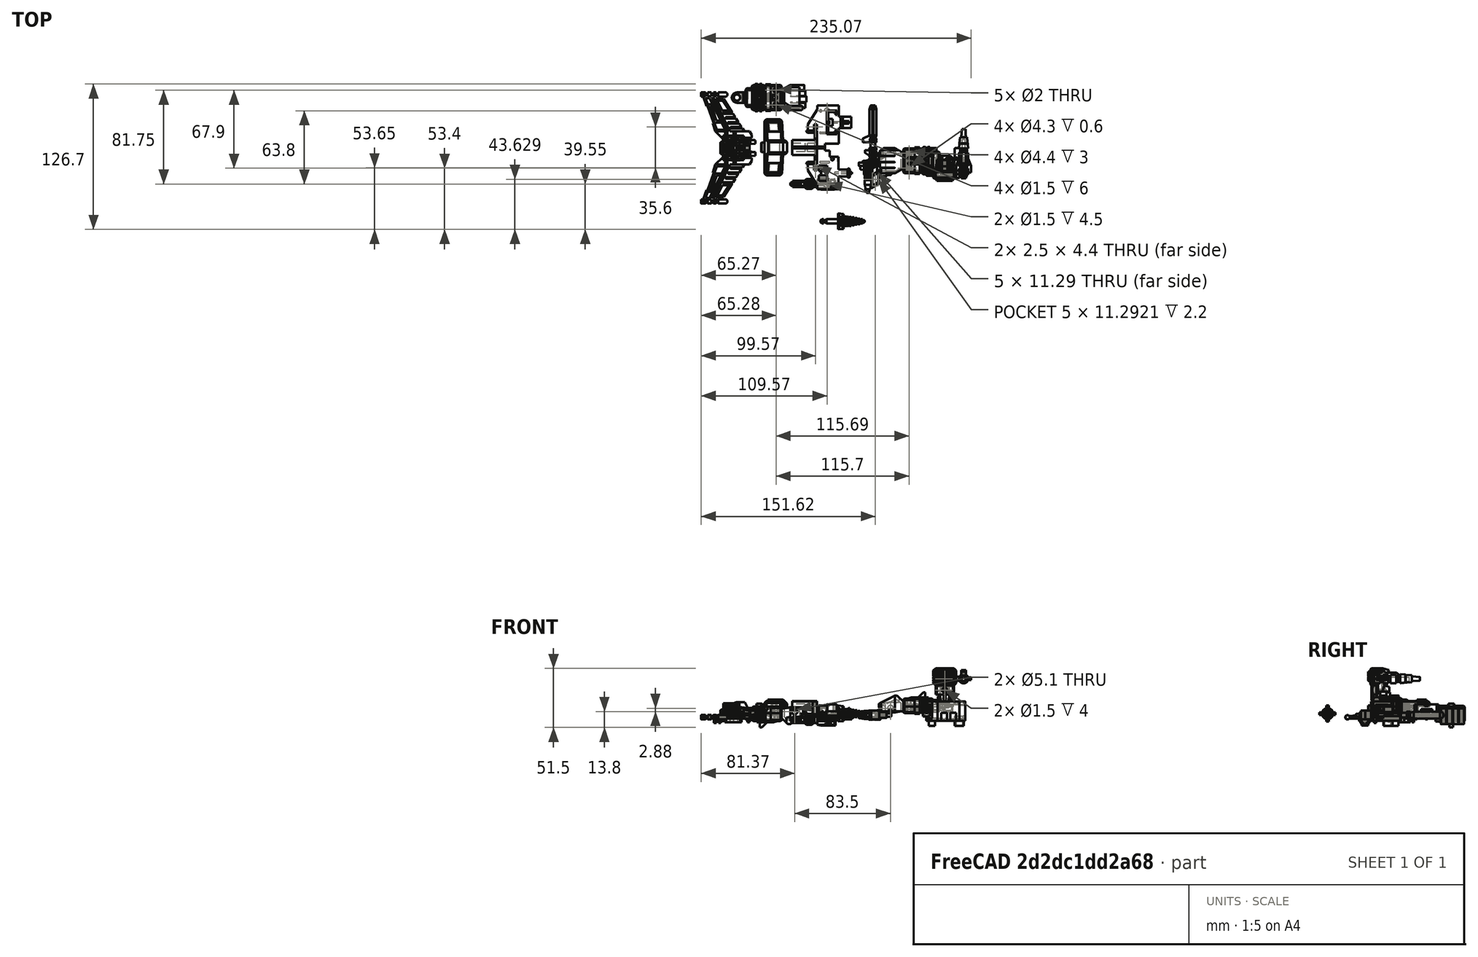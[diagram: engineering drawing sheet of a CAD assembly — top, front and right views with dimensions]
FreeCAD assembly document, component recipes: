
FREECAD ASSEMBLY — COMPONENT RECIPES ("Accesories2")

This assembly document has 7 components, labeled P0..P6 below (a component is one placed body or linked part). 2 of them carry a construction recipe — the FreeCAD feature program that regenerates the part from scratch, quoted from this document or its linked companion documents; the rest are supplied as boundary geometry only. No exploded tour is included for this assembly.
COMPONENT P0 — recipe-attached ("Waist", modeled in this document).
Construction recipe (the document's own serialized feature program — sketch geometry with constraints, then the solid features built on it; lengths are millimeters unless a unit is written):

FEATURE [Sketcher::SketchObject] Sketch571
  ArcFitTolerance = 1e-06
  AttachmentSupport = -> [XY_Plane035]
  FullyConstrained = true
  MakeInternals = false
  MapMode = 5
  sketch-geometry (4):
    g0: LineSegment StartX=0 StartY=0 StartZ=0 EndX=49 EndY=0 EndZ=0
    g1: LineSegment StartX=49 StartY=0 StartZ=0 EndX=49 EndY=15 EndZ=0
    g2: LineSegment StartX=49 StartY=15 StartZ=0 EndX=0 EndY=15 EndZ=0
    g3: LineSegment StartX=0 StartY=15 StartZ=0 EndX=0 EndY=0 EndZ=0
  constraints (11):
    c: Coincident(g0,g1)
    c: Coincident(g1,g2)
    c: Coincident(g2,g3)
    c: Coincident(g3,g0)
    c: Horizontal(g0)
    c: Horizontal(g2)
    c: Vertical(g1)
    c: Vertical(g3)
    c: Coincident(g0,g-1)
    c: DistanceY(g3,g3) = 15
    c: DistanceX(g2,g2) = 49
FEATURE [PartDesign::Pad] Pad410
  Direction = (0,0,1)
  Length = 4.75
  Length2 = 10
  Profile = -> Sketch571
  ReferenceAxis = -> Sketch571 [N_Axis]
  Refine = true
  Suppressed = false
  Type = 0
FEATURE [Sketcher::SketchObject] Sketch572
  ArcFitTolerance = 1e-06
  AttachmentSupport = -> [Pad410]
  ExternalGeometry = -> [Pad410]
  FullyConstrained = true
  MakeInternals = false
  MapMode = 5
  Placement = pos=(0,0,4.75) rot=(0,0,1;0rad)
  sketch-geometry (4):
    g0: LineSegment StartX=0 StartY=0 StartZ=0 EndX=18.55 EndY=-1.3 EndZ=0
    g1: LineSegment StartX=18.55 StartY=-1.3 StartZ=0 EndX=30.45 EndY=-1.3 EndZ=0
    g2: LineSegment StartX=30.45 StartY=-1.3 StartZ=0 EndX=49 EndY=0 EndZ=0
    g3: LineSegment StartX=0 StartY=0 StartZ=0 EndX=49 EndY=0 EndZ=0
  constraints (11):
    c: Coincident(g0,g-1)
    c: Coincident(g1,g0)
    c: Horizontal(g1)
    c: Coincident(g2,g1)
    c: Coincident(g2,g-3)
    c: DistanceY(g0,g0) = 1.3
    c: DistanceX(g1,g1) = 11.9
    c: DistanceX(g0,g2) = 49
    c: DistanceX(g0,g0) = 18.55
    c: Coincident(g3,g0)
    c: Coincident(g3,g2)
FEATURE [PartDesign::Pad] Pad411
  BaseFeature = -> Pad410
  Direction = (0,0,1)
  Length = 4.75
  Length2 = 10
  Profile = -> Sketch572
  ReferenceAxis = -> Sketch572 [N_Axis]
  Refine = true
  Reversed = true
  Suppressed = false
  Type = 0
FEATURE [Sketcher::SketchObject] Sketch573
  ArcFitTolerance = 1e-06
  AttachmentSupport = -> [Pad411]
  ExternalGeometry = -> [Pad411]
  FullyConstrained = true
  MakeInternals = false
  MapMode = 5
  Placement = pos=(0,0,4.75) rot=(0,0,1;0rad)
  sketch-geometry (4):
    g0: LineSegment StartX=18.55 StartY=-4.7 StartZ=0 EndX=30.45 EndY=-4.7 EndZ=0
    g1: LineSegment StartX=30.45 StartY=-4.7 StartZ=0 EndX=30.45 EndY=15 EndZ=0
    g2: LineSegment StartX=30.45 StartY=15 StartZ=0 EndX=18.55 EndY=15 EndZ=0
    g3: LineSegment StartX=18.55 StartY=15 StartZ=0 EndX=18.55 EndY=-4.7 EndZ=0
  constraints (12):
    c: Coincident(g0,g1)
    c: Coincident(g1,g2)
    c: Coincident(g2,g3)
    c: Coincident(g3,g0)
    c: Horizontal(g0)
    c: Horizontal(g2)
    c: Vertical(g1)
    c: Vertical(g3)
    c: PointOnObject(g1,g-4)
    c: PointOnObject(g-3,g3)
    c: PointOnObject(g-3,g1)
    c: DistanceY(g3,g3) = 19.7
FEATURE [PartDesign::Pad] Pad412
  BaseFeature = -> Pad411
  Direction = (0,0,1)
  Length = 4.75
  Length2 = 10
  Profile = -> Sketch573
  ReferenceAxis = -> Sketch573 [N_Axis]
  Refine = true
  Reversed = true
  Suppressed = false
  Type = 0
FEATURE [PartDesign::Pad] Pad413
  BaseFeature = -> Pad412
  Direction = (0,0,1)
  Length = 1.5
  Length2 = 10
  Profile = -> Sketch573
  ReferenceAxis = -> Sketch573 [N_Axis]
  Refine = true
  Suppressed = false
  Type = 0
FEATURE [Sketcher::SketchObject] Sketch574
  ArcFitTolerance = 1e-06
  AttachmentSupport = -> [Pad413]
  ExternalGeometry = -> [Pad413]
  FullyConstrained = true
  MakeInternals = false
  MapMode = 5
  Placement = pos=(0,0,4.75) rot=(0,0,1;0rad)
  sketch-geometry (6):
    g0: LineSegment StartX=0 StartY=15 StartZ=0 EndX=18.55 EndY=15 EndZ=0
    g1: LineSegment StartX=30.45 StartY=15 StartZ=0 EndX=49 EndY=15 EndZ=0
    g2: LineSegment StartX=49 StartY=15 StartZ=0 EndX=30.45 EndY=14 EndZ=0
    g3: LineSegment StartX=30.45 StartY=14 StartZ=0 EndX=30.45 EndY=15 EndZ=0
    g4: LineSegment StartX=0 StartY=15 StartZ=0 EndX=18.55 EndY=14 EndZ=0
    g5: LineSegment StartX=18.55 StartY=14 StartZ=0 EndX=18.55 EndY=15 EndZ=0
  constraints (14):
    c: Coincident(g0,g-3)
    c: Coincident(g0,g-5)
    c: Coincident(g1,g-6)
    c: Coincident(g1,g-4)
    c: Coincident(g2,g1)
    c: PointOnObject(g2,g-6)
    c: Coincident(g3,g2)
    c: Coincident(g3,g1)
    c: Coincident(g4,g0)
    c: PointOnObject(g4,g-5)
    c: Coincident(g5,g4)
    c: Coincident(g5,g0)
    c: DistanceY(g5,g5) = 1
    c: DistanceY(g3,g3) = 1
FEATURE [PartDesign::Pocket] Pocket255
  BaseFeature = -> Pad413
  Direction = (0,0,-1)
  Length = 3.25
  Length2 = 5
  Profile = -> Sketch574
  ReferenceAxis = -> Sketch574 [N_Axis]
  Refine = true
  Suppressed = false
  Type = 0
FEATURE [Sketcher::SketchObject] Sketch575
  ArcFitTolerance = 1e-06
  AttachmentSupport = -> [Pocket255]
  ExternalGeometry = -> [Pocket255]
  FullyConstrained = true
  MakeInternals = false
  MapMode = 5
  Placement = pos=(0,0,4.75) rot=(0,0,1;0rad)
  sketch-geometry (12):
    g0: LineSegment StartX=2.7 StartY=12.1505 StartZ=0 EndX=10.95 EndY=11.7058 EndZ=0
    g1: LineSegment StartX=10.95 StartY=11.7058 StartZ=0 EndX=10.95 EndY=1.93924 EndZ=0
    g2: LineSegment StartX=10.95 StartY=1.93924 StartZ=0 EndX=2.7 EndY=2.5174 EndZ=0
    g3: LineSegment StartX=2.7 StartY=2.5174 StartZ=0 EndX=2.7 EndY=12.1505 EndZ=0
    g4: LineSegment StartX=46.3 StartY=12.1505 StartZ=0 EndX=38.05 EndY=11.7058 EndZ=0
    g5: LineSegment StartX=38.05 StartY=11.7058 StartZ=0 EndX=38.05 EndY=1.93924 EndZ=0
    g6: LineSegment StartX=38.05 StartY=1.93924 StartZ=0 EndX=46.3 EndY=2.5174 EndZ=0
    g7: LineSegment StartX=46.3 StartY=2.5174 StartZ=0 EndX=46.3 EndY=12.1505 EndZ=0
    g8: LineSegment [constr] StartX=40.9003 StartY=14.5634 StartZ=0 EndX=41.0457 EndY=11.8673 EndZ=0
    g9: LineSegment [constr] StartX=8.09969 StartY=14.5634 StartZ=0 EndX=7.95435 EndY=11.8673 EndZ=0
    g10: LineSegment [constr] StartX=7.95734 StartY=2.14896 StartZ=0 EndX=7.76858 EndY=-0.544429 EndZ=0
    g11: LineSegment [constr] StartX=41.0427 StartY=2.14896 StartZ=0 EndX=41.2314 EndY=-0.544429 EndZ=0
  constraints (40):
    c: Coincident(g1,g0)
    c: Vertical(g1)
    c: Coincident(g2,g1)
    c: Coincident(g3,g2)
    c: Coincident(g3,g0)
    c: Coincident(g5,g4)
    c: Vertical(g5)
    c: Coincident(g6,g5)
    c: Coincident(g7,g6)
    c: Coincident(g7,g4)
    c: Vertical(g7)
    c: Vertical(g3)
    c: Parallel(g-3,g0)
    c: Parallel(g-6,g2)
    c: Parallel(g4,g-4)
    c: Parallel(g6,g-5)
    c: DistanceX(g0,g0) = 8.25
    c: DistanceX(g4,g4) = 8.25
    c: DistanceX(g-3,g0) = 2.7
    c: DistanceX(g4,g-4) = 2.7
    c: PointOnObject(g8,g-4)
    c: PointOnObject(g8,g4)
    c: PointOnObject(g9,g-3)
    c: PointOnObject(g9,g0)
    c: Perpendicular(g9,g-3)
    c: Perpendicular(g8,g-4)
    c: Distance(g4,g8) = 3
    c: Distance(g0,g9) = 3
    c: Distance(g9) = 2.7
    c: Distance(g8) = 2.7
    c: PointOnObject(g10,g2)
    c: PointOnObject(g10,g-6)
    c: Perpendicular(g-6,g10)
    c: Distance(g10) = 2.7
    c: PointOnObject(g11,g6)
    c: PointOnObject(g11,g-5)
    c: Perpendicular(g11,g6)
    c: Distance(g11) = 2.7
    c: Distance(g5,g11) = 3
    c: Distance(g10,g1) = 3
FEATURE [PartDesign::Pad] Pad414
  BaseFeature = -> Pocket255
  Direction = (0,0,1)
  Length = 1.5
  Length2 = 10
  Profile = -> Sketch575
  ReferenceAxis = -> Sketch575 [N_Axis]
  Refine = true
  Suppressed = false
  Type = 0
FEATURE [PartDesign::Chamfer] Chamfer010
  Angle = 45
  Base = -> Pad414 [Edge3,Edge2,Edge29,Edge30,Edge52,Edge31,Edge43,Edge17,Edge5,Edge14]
  BaseFeature = -> Pad414
  ChamferType = 0
  FlipDirection = false
  Refine = true
  Size = 1.5
  Size2 = 1
  SupportTransform = false
  Suppressed = false
  UseAllEdges = false
FEATURE [PartDesign::Chamfer] Chamfer011
  Angle = 45
  Base = -> Chamfer010 [Edge48,Edge21]
  BaseFeature = -> Chamfer010
  ChamferType = 0
  FlipDirection = false
  Refine = true
  Size = 3.5
  Size2 = 1
  SupportTransform = false
  Suppressed = false
  UseAllEdges = false
FEATURE [PartDesign::Chamfer] Chamfer012
  Angle = 45
  Base = -> Chamfer011 [Edge26,Edge28,Edge30,Edge15,Edge13,Edge11]
  BaseFeature = -> Chamfer011
  ChamferType = 0
  FlipDirection = false
  Refine = true
  Size = 1.49
  Size2 = 1
  SupportTransform = false
  Suppressed = false
  UseAllEdges = false
FEATURE [Sketcher::SketchObject] Sketch576
  ArcFitTolerance = 1e-06
  AttachmentSupport = -> [Chamfer012]
  ExternalGeometry = -> [Chamfer012]
  FullyConstrained = true
  MakeInternals = false
  MapMode = 5
  Placement = pos=(0,0,1.5) rot=(0,0,1;0rad)
  sketch-geometry (6):
    g0: LineSegment StartX=0 StartY=13.5 StartZ=0 EndX=1.58304 EndY=15 EndZ=0
    g1: LineSegment StartX=1.58304 StartY=15 StartZ=0 EndX=0 EndY=15 EndZ=0
    g2: LineSegment StartX=0 StartY=15 StartZ=0 EndX=0 EndY=13.5 EndZ=0
    g3: LineSegment StartX=49 StartY=13.5 StartZ=0 EndX=47.417 EndY=15 EndZ=0
    g4: LineSegment StartX=47.417 StartY=15 StartZ=0 EndX=49 EndY=15 EndZ=0
    g5: LineSegment StartX=49 StartY=15 StartZ=0 EndX=49 EndY=13.5 EndZ=0
  constraints (14):
    c: Coincident(g0,g-5)
    c: PointOnObject(g0,g-3)
    c: PointOnObject(g-4,g0)
    c: Coincident(g1,g0)
    c: Coincident(g1,g-5)
    c: Coincident(g2,g1)
    c: Coincident(g2,g0)
    c: Coincident(g3,g-9)
    c: PointOnObject(g3,g-7)
    c: Coincident(g4,g3)
    c: Coincident(g4,g-8)
    c: Coincident(g5,g4)
    c: Coincident(g5,g3)
    c: PointOnObject(g-6,g3)
FEATURE [PartDesign::Pocket] Pocket256
  BaseFeature = -> Chamfer012
  Direction = (0,0,-1)
  Length = 5
  Length2 = 5
  Profile = -> Sketch576
  ReferenceAxis = -> Sketch576 [N_Axis]
  Refine = true
  Suppressed = false
  Type = 0
FEATURE [Sketcher::SketchObject] Sketch577
  ArcFitTolerance = 1e-06
  AttachmentSupport = -> [Pocket256]
  ExternalGeometry = -> [Pocket256]
  FullyConstrained = true
  MakeInternals = false
  MapMode = 5
  Placement = pos=(0,0,0) rot=(1,0,0;3.14159rad)
  sketch-geometry (4):
    g0: LineSegment StartX=1.5 StartY=-1.39856 StartZ=0 EndX=1.5 EndY=-12.4978 EndZ=0
    g1: LineSegment StartX=1.5 StartY=-12.4978 StartZ=0 EndX=47.5 EndY=-12.4978 EndZ=0
    g2: LineSegment StartX=47.5 StartY=-12.4978 StartZ=0 EndX=47.5 EndY=-1.39856 EndZ=0
    g3: LineSegment StartX=47.5 StartY=-1.39856 StartZ=0 EndX=1.5 EndY=-1.39856 EndZ=0
  constraints (10):
    c: Coincident(g0,g1)
    c: Coincident(g1,g2)
    c: Coincident(g2,g3)
    c: Coincident(g3,g0)
    c: Vertical(g0)
    c: Vertical(g2)
    c: Horizontal(g1)
    c: Coincident(g0,g-8)
    c: PointOnObject(g-4,g1)
    c: Coincident(g2,g-7)
FEATURE [PartDesign::Pocket] Pocket257
  BaseFeature = -> Pocket256
  Direction = (0,0,1)
  Length = 3.25
  Length2 = 5
  Profile = -> Sketch577
  ReferenceAxis = -> Sketch577 [N_Axis]
  Refine = true
  Suppressed = false
  Type = 0
FEATURE [Sketcher::SketchObject] Sketch578
  ArcFitTolerance = 1e-06
  AttachmentSupport = -> [Pocket257]
  ExternalGeometry = -> [Pocket257]
  FullyConstrained = true
  MakeInternals = false
  MapMode = 5
  Placement = pos=(0,0,0) rot=(1,0,0;3.14159rad)
  sketch-geometry (4):
    g0: LineSegment StartX=20.04 StartY=1.2 StartZ=0 EndX=20.04 EndY=-1.39856 EndZ=0
    g1: LineSegment StartX=20.04 StartY=-1.39856 StartZ=0 EndX=28.96 EndY=-1.39856 EndZ=0
    g2: LineSegment StartX=28.96 StartY=-1.39856 StartZ=0 EndX=28.96 EndY=1.2 EndZ=0
    g3: LineSegment StartX=28.96 StartY=1.2 StartZ=0 EndX=20.04 EndY=1.2 EndZ=0
  constraints (10):
    c: Coincident(g0,g1)
    c: Coincident(g1,g2)
    c: Coincident(g2,g3)
    c: Coincident(g3,g0)
    c: Vertical(g0)
    c: Vertical(g2)
    c: Horizontal(g1)
    c: Coincident(g0,g-3)
    c: PointOnObject(g1,g-4)
    c: Coincident(g2,g-3)
FEATURE [PartDesign::Pocket] Pocket258
  BaseFeature = -> Pocket257
  Direction = (0,0,1)
  Length = 3.25
  Length2 = 5
  Profile = -> Sketch578
  ReferenceAxis = -> Sketch578 [N_Axis]
  Refine = true
  Suppressed = false
  Type = 0
FEATURE [Sketcher::SketchObject] Sketch579
  ArcFitTolerance = 1e-06
  AttachmentSupport = -> [Pocket258]
  ExternalGeometry = -> [Pocket258]
  FullyConstrained = true
  MakeInternals = false
  MapMode = 5
  Placement = pos=(0,0,3.25) rot=(1,0,0;3.14159rad)
  sketch-geometry (12):
    g0: LineSegment StartX=20.04 StartY=1.2 StartZ=0 EndX=20.04 EndY=-12.4978 EndZ=0
    g1: LineSegment StartX=20.04 StartY=-12.4978 StartZ=0 EndX=28.96 EndY=-12.4978 EndZ=0
    g2: LineSegment StartX=28.96 StartY=-12.4978 StartZ=0 EndX=28.96 EndY=1.2 EndZ=0
    g3: LineSegment StartX=28.96 StartY=1.2 StartZ=0 EndX=20.04 EndY=1.2 EndZ=0
    g4: LineSegment StartX=3.7 StartY=-3.27724 StartZ=0 EndX=9.95 EndY=-2.83924 EndZ=0
    g5: LineSegment StartX=9.95 StartY=-2.83924 StartZ=0 EndX=9.95 EndY=-10.8058 EndZ=0
    g6: LineSegment StartX=9.95 StartY=-10.8058 StartZ=0 EndX=3.7 EndY=-11.1427 EndZ=0
    g7: LineSegment StartX=3.7 StartY=-11.1427 StartZ=0 EndX=3.7 EndY=-3.27724 EndZ=0
    g8: LineSegment StartX=39.05 StartY=-2.83924 StartZ=0 EndX=45.3 EndY=-3.27724 EndZ=0
    g9: LineSegment StartX=45.3 StartY=-3.27724 StartZ=0 EndX=45.3 EndY=-11.1427 EndZ=0
    g10: LineSegment StartX=45.3 StartY=-11.1427 StartZ=0 EndX=39.05 EndY=-10.8058 EndZ=0
    g11: LineSegment StartX=39.05 StartY=-10.8058 StartZ=0 EndX=39.05 EndY=-2.83924 EndZ=0
  constraints (34):
    c: Coincident(g0,g1)
    c: Coincident(g1,g2)
    c: Coincident(g2,g3)
    c: Coincident(g3,g0)
    c: Vertical(g0)
    c: Vertical(g2)
    c: Horizontal(g1)
    c: Coincident(g0,g-7)
    c: PointOnObject(g1,g-6)
    c: Coincident(g2,g-7)
    c: Coincident(g5,g4)
    c: Vertical(g5)
    c: Coincident(g6,g5)
    c: Coincident(g7,g6)
    c: Coincident(g7,g4)
    c: Vertical(g7)
    c: Coincident(g9,g8)
    c: Vertical(g9)
    c: Coincident(g10,g9)
    c: Coincident(g11,g10)
    c: Coincident(g11,g8)
    c: Vertical(g11)
    c: DistanceX(g-15,g8) = 1
    c: DistanceX(g8,g-15) = 1
    c: DistanceX(g4,g-9) = 1
    c: DistanceX(g-10,g4) = 1
    c: Parallel(g-8,g4)
    c: Parallel(g6,g-11)
    c: Parallel(g8,g-15)
    c: Parallel(g10,g-14)
    c: DistanceY(g-14,g10) = 0.9
    c: DistanceY(g8,g-15) = 0.9
    c: DistanceY(g4,g-9) = 0.9
    c: DistanceY(g-11,g5) = 0.9
FEATURE [PartDesign::Pocket] Pocket259
  BaseFeature = -> Pocket258
  Direction = (0,0,1)
  Length = 1.5
  Length2 = 5
  Profile = -> Sketch579
  ReferenceAxis = -> Sketch579 [N_Axis]
  Refine = true
  Suppressed = false
  Type = 0
FEATURE [Sketcher::SketchObject] Sketch580
  ArcFitTolerance = 1e-06
  AttachmentSupport = -> [Pocket259]
  ExternalGeometry = -> [Pocket259]
  FullyConstrained = true
  MakeInternals = false
  MapMode = 5
  Placement = pos=(20.04,0,0) rot=(0.57735,0.57735,0.57735;2.0944rad)
  sketch-geometry (3):
    g0: LineSegment StartX=-1.2 StartY=4.75 StartZ=0 EndX=-1.2 EndY=1.75 EndZ=0
    g1: LineSegment StartX=-1.2 StartY=1.75 StartZ=0 EndX=1.8 EndY=4.75 EndZ=0
    g2: LineSegment StartX=1.8 StartY=4.75 StartZ=0 EndX=-1.2 EndY=4.75 EndZ=0
  constraints (8):
    c: Coincident(g0,g-4)
    c: PointOnObject(g1,g-4)
    c: Coincident(g2,g1)
    c: Coincident(g2,g0)
    c: Angle(g1,g0) = 0.785398
    c: Coincident(g0,g1)
    c: PointOnObject(g0,g-3)
    c: DistanceY(g0,g0) = 3
FEATURE [PartDesign::Pad] Pad415
  BaseFeature = -> Pocket259
  Direction = (1,0,0)
  Length = 9
  Length2 = 10
  Profile = -> Sketch580
  ReferenceAxis = -> Sketch580 [N_Axis]
  Refine = true
  Suppressed = false
  Type = 0
FEATURE [Sketcher::SketchObject] Sketch581
  ArcFitTolerance = 1e-06
  AttachmentSupport = -> [Pad415]
  ExternalGeometry = -> [Pad415]
  FullyConstrained = true
  MakeInternals = false
  MapMode = 5
  Placement = pos=(28.96,0,0) rot=(0.57735,-0.57735,-0.57735;2.0944rad)
  sketch-geometry (3):
    g0: LineSegment StartX=-12.4978 StartY=4.75 StartZ=0 EndX=-12.4978 EndY=2.75 EndZ=0
    g1: LineSegment StartX=-12.4978 StartY=2.75 StartZ=0 EndX=-10.4978 EndY=4.75 EndZ=0
    g2: LineSegment StartX=-10.4978 StartY=4.75 StartZ=0 EndX=-12.4978 EndY=4.75 EndZ=0
  constraints (8):
    c: Coincident(g0,g-4)
    c: PointOnObject(g-3,g0)
    c: Coincident(g1,g0)
    c: PointOnObject(g1,g-4)
    c: Coincident(g2,g1)
    c: Coincident(g2,g0)
    c: Angle(g1,g0) = 0.785398
    c: DistanceY(g0,g0) = 2
FEATURE [PartDesign::Pad] Pad416
  BaseFeature = -> Pad415
  Direction = (-1,0,0)
  Length = 28
  Length2 = 10
  Profile = -> Sketch581
  ReferenceAxis = -> Sketch581 [N_Axis]
  Refine = true
  Suppressed = false
  Type = 0
FEATURE [PartDesign::Pad] Pad417
  BaseFeature = -> Pad416
  Direction = (1,0,0)
  Length = 20
  Length2 = 10
  Profile = -> Pad416 [Face52]
  Refine = true
  Suppressed = false
  Type = 0
FEATURE [PartDesign::Pocket] Pocket260
  BaseFeature = -> Pad417
  Direction = (0,-1,-1.8e-15)
  Length = 5
  Length2 = 5
  Profile = -> Pad417 [Face56]
  Refine = true
  Suppressed = false
  Type = 0
FEATURE [Sketcher::SketchObject] Sketch582
  ArcFitTolerance = 1e-06
  AttachmentSupport = -> [Pocket260]
  ExternalGeometry = -> [Pocket260]
  FullyConstrained = true
  MakeInternals = false
  MapMode = 5
  Placement = pos=(0,0,3.25) rot=(1,0,0;3.14159rad)
  sketch-geometry (4):
    g0: LineSegment StartX=3.7 StartY=-3.27724 StartZ=0 EndX=9.95 EndY=-2.83924 EndZ=0
    g1: LineSegment StartX=9.95 StartY=-2.83924 StartZ=0 EndX=9.95 EndY=-10.8058 EndZ=0
    g2: LineSegment StartX=9.95 StartY=-10.8058 StartZ=0 EndX=3.7 EndY=-11.1427 EndZ=0
    g3: LineSegment StartX=3.7 StartY=-11.1427 StartZ=0 EndX=3.7 EndY=-3.27724 EndZ=0
  constraints (8):
    c: Coincident(g0,g-4)
    c: Coincident(g0,g-5)
    c: Coincident(g1,g0)
    c: Coincident(g1,g-6)
    c: Coincident(g2,g1)
    c: Coincident(g2,g-6)
    c: Coincident(g3,g2)
    c: Coincident(g3,g0)
FEATURE [PartDesign::Pocket] Pocket261
  BaseFeature = -> Pocket260
  Direction = (0,0,1)
  Length = 1.5
  Length2 = 5
  Profile = -> Sketch582
  ReferenceAxis = -> Sketch582 [N_Axis]
  Refine = true
  Suppressed = false
  Type = 0
FEATURE [Sketcher::SketchObject] Sketch583
  ArcFitTolerance = 1e-06
  AttachmentSupport = -> [Pocket261]
  ExternalGeometry = -> [Pocket261]
  FullyConstrained = true
  MakeInternals = false
  MapMode = 5
  Placement = pos=(0,0,0) rot=(1,0,0;3.14159rad)
  sketch-geometry (4):
    g0: Circle CenterX=32.3 CenterY=-13.7478 CenterZ=0 NormalX=0 NormalY=0 NormalZ=1 AngleXU=0 Radius=1.25
    g1: Circle CenterX=16.7 CenterY=-13.7478 CenterZ=0 NormalX=0 NormalY=0 NormalZ=1 AngleXU=0 Radius=1.25
    g2: LineSegment [constr] StartX=16.7 StartY=-13.7478 StartZ=0 EndX=17.95 EndY=-13.7478 EndZ=0
    g3: LineSegment [constr] StartX=32.3 StartY=-13.7478 StartZ=0 EndX=31.05 EndY=-13.7478 EndZ=0
  constraints (16):
    c: DistanceY(g-4,g-3) = 2.50218
    c: Diameter(g1) = 2.5
    c: Diameter(g0) = 2.5
    c: Tangent(g0,g-3)
    c: Tangent(g1,g-3)
    c: DistanceX(g-5,g-6) = 8.92
    c: DistanceX(g1,g0) = 15.6
    c: Coincident(g2,g1)
    c: PointOnObject(g2,g1)
    c: Horizontal(g2)
    c: Coincident(g3,g0)
    c: PointOnObject(g3,g0)
    c: Horizontal(g3)
    c: DistanceX(g2,g3) = 13.1
    c: DistanceX(g2,g-5) = 2.09
    c: DistanceX(g-6,g3) = 2.09
FEATURE [PartDesign::Pad] Pad418
  BaseFeature = -> Pocket261
  Direction = (0,0,-1)
  Length = 3
  Length2 = 10
  Profile = -> Sketch583
  ReferenceAxis = -> Sketch583 [N_Axis]
  Refine = true
  Suppressed = false
  Type = 0
FEATURE [Sketcher::SketchObject] Sketch584
  ArcFitTolerance = 1e-06
  AttachmentSupport = -> [Pad418]
  ExternalGeometry = -> [Pad418]
  FullyConstrained = true
  MakeInternals = false
  MapMode = 5
  Placement = pos=(0,15,0) rot=(0,0.707107,0.707107;3.14159rad)
  sketch-geometry (4):
    g0: LineSegment StartX=-28.55 StartY=2 StartZ=0 EndX=-28.55 EndY=0 EndZ=0
    g1: LineSegment StartX=-28.55 StartY=0 StartZ=0 EndX=-20.45 EndY=0 EndZ=0
    g2: LineSegment StartX=-20.45 StartY=0 StartZ=0 EndX=-20.45 EndY=2 EndZ=0
    g3: LineSegment StartX=-20.45 StartY=2 StartZ=0 EndX=-28.55 EndY=2 EndZ=0
  constraints (13):
    c: Coincident(g0,g1)
    c: Coincident(g1,g2)
    c: Coincident(g2,g3)
    c: Coincident(g3,g0)
    c: Vertical(g0)
    c: Vertical(g2)
    c: Horizontal(g1)
    c: Horizontal(g3)
    c: DistanceX(g3,g3) = 8.1
    c: DistanceY(g0,g0) = 2
    c: DistanceX(g-3,g-3) = 11.9
    c: DistanceX(g-3,g0) = 1.9
    c: PointOnObject(g0,g-4)
FEATURE [PartDesign::Pad] Pad419
  BaseFeature = -> Pad418
  Direction = (0,1,-2e-16)
  Length = 2.75
  Length2 = 10
  Profile = -> Sketch584
  ReferenceAxis = -> Sketch584 [N_Axis]
  Refine = true
  Suppressed = false
  Type = 0
FEATURE [Sketcher::SketchObject] Sketch585
  ArcFitTolerance = 1e-06
  AttachmentSupport = -> [Pad419]
  ExternalGeometry = -> [Pad419]
  FullyConstrained = true
  MakeInternals = false
  MapMode = 5
  Placement = pos=(28.55,0,0) rot=(0.57735,0.57735,0.57735;2.0944rad)
  sketch-geometry (3):
    g0: LineSegment StartX=15 StartY=2 StartZ=0 EndX=17.75 EndY=2 EndZ=0
    g1: LineSegment StartX=17.75 StartY=2 StartZ=0 EndX=15 EndY=2.1 EndZ=0
    g2: LineSegment StartX=15 StartY=2.1 StartZ=0 EndX=15 EndY=2 EndZ=0
  constraints (7):
    c: Coincident(g0,g-3)
    c: Coincident(g0,g-3)
    c: Coincident(g1,g0)
    c: PointOnObject(g1,g-4)
    c: Coincident(g2,g1)
    c: Coincident(g2,g0)
    c: DistanceY(g2,g2) = 0.1
FEATURE [PartDesign::Pad] Pad420
  BaseFeature = -> Pad419
  Direction = (1,0,0)
  Length = 8.1
  Length2 = 10
  Profile = -> Sketch585
  ReferenceAxis = -> Sketch585 [N_Axis]
  Refine = true
  Reversed = true
  Suppressed = false
  Type = 0
FEATURE [Sketcher::SketchObject] Sketch586
  ArcFitTolerance = 1e-06
  AttachmentSupport = -> [Pad420]
  ExternalGeometry = -> [Pad420]
  FullyConstrained = true
  MakeInternals = false
  MapMode = 5
  Placement = pos=(0,0,0) rot=(1,0,0;3.14159rad)
  sketch-geometry (6):
    g0: LineSegment StartX=28.55 StartY=-15 StartZ=0 EndX=28.55 EndY=-17.75 EndZ=0
    g1: LineSegment StartX=28.55 StartY=-17.75 StartZ=0 EndX=28.6 EndY=-15 EndZ=0
    g2: LineSegment StartX=28.6 StartY=-15 StartZ=0 EndX=28.55 EndY=-15 EndZ=0
    g3: LineSegment StartX=20.45 StartY=-17.75 StartZ=0 EndX=20.45 EndY=-15 EndZ=0
    g4: LineSegment StartX=20.45 StartY=-17.75 StartZ=0 EndX=20.4 EndY=-15 EndZ=0
    g5: LineSegment StartX=20.45 StartY=-15 StartZ=0 EndX=20.4 EndY=-15 EndZ=0
  constraints (14):
    c: Coincident(g0,g-4)
    c: Coincident(g0,g-4)
    c: Coincident(g1,g0)
    c: PointOnObject(g1,g-3)
    c: Coincident(g2,g1)
    c: Coincident(g2,g0)
    c: DistanceX(g2,g2) = 0.05
    c: Coincident(g3,g-5)
    c: Coincident(g3,g-6)
    c: Coincident(g4,g3)
    c: PointOnObject(g4,g-6)
    c: Coincident(g5,g3)
    c: Coincident(g5,g4)
    c: DistanceX(g5,g5) = 0.05
FEATURE [PartDesign::Pad] Pad421
  BaseFeature = -> Pad420
  Direction = (0,0,-1)
  Length = 3
  Length2 = 10
  Profile = -> Sketch586
  ReferenceAxis = -> Sketch586 [N_Axis]
  Refine = true
  Reversed = true
  Suppressed = false
  Type = 0
FEATURE [PartDesign::Pocket] Pocket262
  BaseFeature = -> Pad421
  Direction = (-1,2.6e-15,0)
  Length = 5
  Length2 = 5
  Profile = -> Pad421 [Face41]
  Refine = true
  Suppressed = false
  Type = 0
FEATURE [PartDesign::Pocket] Pocket263
  BaseFeature = -> Pocket262
  Direction = (1,-2.6e-15,0)
  Length = 5
  Length2 = 5
  Profile = -> Pocket262 [Face48]
  Refine = true
  Suppressed = false
  Type = 0
FEATURE [PartDesign::Chamfer] Chamfer013
  Angle = 45
  Base = -> Pocket263 [Edge106,Edge105,Edge38,Edge83]
  BaseFeature = -> Pocket263
  ChamferType = 0
  FlipDirection = false
  Refine = true
  Size = 0.3
  Size2 = 1
  SupportTransform = false
  Suppressed = false
  UseAllEdges = false
FEATURE [PartDesign::Body] Body032  label="Waist"
  AllowCompound = false
  Group = -> [Sketch571,Pad410,Sketch572,Pad411,Sketch573,Pad412,Pad413,Sketch574,Pocket255,Sketch575,Pad414,Chamfer010,Chamfer011,Chamfer012,Sketch576,Pocket256,Sketch577,Pocket257,Sketch578,Pocket258,Sketch579,Pocket259,Sketch580,Pad415,Sketch581,Pad416,Pad417,Pocket260,Sketch582,Pocket261,Sketch583,Pad418,Sketch584,Pad419,Sketch585,Pad420,Sketch586,Pad421,Pocket262,Pocket263,Chamfer013]
  Origin = -> Origin035
  Placement = pos=(-106,-2,0) rot=(0,0,1;1.5708rad)
  Tip = -> Chamfer013
COMPONENT P1 — geometry summary ("Chestplate"; its construction recipe is too large to include in this document):
  bounding box: 97.0 x 47.2 x 18.2 mm
  tessellated surface: 26,040 triangles
  volume: 7222 mm^3 (9% of its bounding box)
COMPONENT P2 — recipe-attached ("Drill_Fist2", modeled in this document).
Construction recipe (the document's own serialized feature program — sketch geometry with constraints, then the solid features built on it; lengths are millimeters unless a unit is written):

FEATURE [Sketcher::SketchObject] Sketch1064
  ArcFitTolerance = 1e-06
  AttachmentOffset = pos=(-60,-44,0) rot=(0,0,1;0rad)
  AttachmentSupport = -> [XY_Plane058]
  FullyConstrained = true
  MakeInternals = false
  MapMode = 5
  Placement = pos=(-60,-44,0) rot=(0,0,1;0rad)
  sketch-geometry (1):
    g0: Circle CenterX=0 CenterY=0 CenterZ=0 NormalX=0 NormalY=0 NormalZ=1 AngleXU=0 Radius=4.8
  constraints (2):
    c: Coincident(g0,g-1)
    c: Diameter(g0) = 9.6
FEATURE [PartDesign::Pad] Pad691
  Direction = (0,0,1)
  Length = 2
  Length2 = 10
  Profile = -> Sketch1064
  ReferenceAxis = -> Sketch1064 [N_Axis]
  Refine = true
  Suppressed = false
  Type = 0
FEATURE [Sketcher::SketchObject] Sketch1065
  ArcFitTolerance = 1e-06
  AttachmentSupport = -> [Pad691]
  ExternalGeometry = -> [Pad691]
  FullyConstrained = true
  MakeInternals = false
  MapMode = 5
  Placement = pos=(0,0,2) rot=(0,0,1;0rad)
  sketch-geometry (1):
    g0: Circle CenterX=-60 CenterY=-44 CenterZ=0 NormalX=0 NormalY=0 NormalZ=1 AngleXU=0 Radius=2.5
  constraints (2):
    c: Coincident(g0,g-3)
    c: Diameter(g0) = 5
FEATURE [PartDesign::Pad] Pad692
  BaseFeature = -> Pad691
  Direction = (0,0,1)
  Length = 1
  Length2 = 10
  Profile = -> Sketch1065
  ReferenceAxis = -> Sketch1065 [N_Axis]
  Refine = true
  Suppressed = false
  Type = 0
FEATURE [Sketcher::SketchObject] Sketch1066
  ArcFitTolerance = 1e-06
  AttachmentSupport = -> [Pad692]
  ExternalGeometry = -> [Pad692]
  FullyConstrained = true
  MakeInternals = false
  MapMode = 5
  Placement = pos=(0,0,3) rot=(0,0,1;0rad)
  sketch-geometry (1):
    g0: Circle CenterX=-60 CenterY=-44 CenterZ=0 NormalX=0 NormalY=0 NormalZ=1 AngleXU=0 Radius=4.8
  constraints (2):
    c: Coincident(g0,g-4)
    c: Equal(g0,g-4)
FEATURE [PartDesign::Pad] Pad693
  BaseFeature = -> Pad692
  Direction = (0,0,1)
  Length = 2
  Length2 = 10
  Profile = -> Sketch1066
  ReferenceAxis = -> Sketch1066 [N_Axis]
  Refine = true
  Suppressed = false
  Type = 0
FEATURE [Sketcher::SketchObject] Sketch1067
  ArcFitTolerance = 1e-06
  AttachmentSupport = -> [Pad693]
  ExternalGeometry = -> [Pad693]
  FullyConstrained = true
  MakeInternals = false
  MapMode = 5
  Placement = pos=(0,0,0) rot=(1,0,0;3.14159rad)
  sketch-geometry (1):
    g0: Circle CenterX=-60 CenterY=44 CenterZ=0 NormalX=0 NormalY=0 NormalZ=1 AngleXU=0 Radius=1.92
  constraints (2):
    c: Coincident(g0,g-3)
    c: Radius(g0) = 1.92
FEATURE [PartDesign::Pad] Pad694
  BaseFeature = -> Pad693
  Direction = (0,0,-1)
  Length = 11
  Length2 = 10
  Profile = -> Sketch1067
  ReferenceAxis = -> Sketch1067 [N_Axis]
  Refine = true
  Suppressed = false
  Type = 0
FEATURE [Sketcher::SketchObject] Sketch1068
  ArcFitTolerance = 1e-06
  AttachmentSupport = -> [Pad694]
  ExternalGeometry = -> [Pad694]
  FullyConstrained = true
  MakeInternals = false
  MapMode = 5
  Placement = pos=(0,0,-11) rot=(1,0,0;3.14159rad)
  sketch-geometry (1):
    g0: Circle CenterX=-60 CenterY=44 CenterZ=0 NormalX=0 NormalY=0 NormalZ=1 AngleXU=0 Radius=1
  constraints (2):
    c: Coincident(g0,g-3)
    c: Radius(g0) = 1
FEATURE [PartDesign::Pad] Pad695
  BaseFeature = -> Pad694
  Direction = (0,0,-1)
  Length = 1.5
  Length2 = 10
  Profile = -> Sketch1068
  ReferenceAxis = -> Sketch1068 [N_Axis]
  Refine = true
  Suppressed = false
  Type = 0
FEATURE [Sketcher::SketchObject] Sketch1069
  ArcFitTolerance = 1e-06
  AttachmentSupport = -> [Pad695]
  ExternalGeometry = -> [Pad695]
  FullyConstrained = true
  MakeInternals = false
  MapMode = 5
  Placement = pos=(0,0,-12.5) rot=(1,0,0;3.14159rad)
  sketch-geometry (1):
    g0: Circle CenterX=-60 CenterY=44 CenterZ=0 NormalX=0 NormalY=0 NormalZ=1 AngleXU=0 Radius=1.92
  constraints (2):
    c: Coincident(g0,g-4)
    c: Equal(g0,g-4)
FEATURE [PartDesign::Pad] Pad696
  BaseFeature = -> Pad695
  Direction = (0,0,-1)
  Length = 2.5
  Length2 = 10
  Profile = -> Sketch1069
  ReferenceAxis = -> Sketch1069 [N_Axis]
  Refine = true
  Suppressed = false
  Type = 0
FEATURE [PartDesign::Chamfer] Chamfer052
  Angle = 45
  Base = -> Pad696 [Edge18]
  BaseFeature = -> Pad696
  ChamferType = 0
  FlipDirection = false
  Refine = true
  Size = 1
  Size2 = 1
  SupportTransform = false
  Suppressed = false
  UseAllEdges = false
FEATURE [PartDesign::Chamfer] Chamfer053
  Angle = 45
  Base = -> Chamfer052 [Edge9]
  BaseFeature = -> Chamfer052
  ChamferType = 0
  FlipDirection = false
  Refine = true
  Size = 0.9
  Size2 = 1
  SupportTransform = false
  Suppressed = false
  UseAllEdges = false
FEATURE [Sketcher::SketchObject] Sketch1070
  ArcFitTolerance = 1e-06
  AttachmentOffset = pos=(0,0,45) rot=(0,0,1;0rad)
  AttachmentSupport = -> [XZ_Plane058]
  ExternalGeometry = -> [Chamfer053]
  FullyConstrained = true
  MakeInternals = false
  MapMode = 5
  Placement = pos=(0,-45,1e-14) rot=(1,0,0;1.5708rad)
  sketch-geometry (8):
    g0: LineSegment StartX=-53 StartY=5 StartZ=0 EndX=-58.2 EndY=5 EndZ=0
    g1: LineSegment StartX=-58.2 StartY=5 StartZ=0 EndX=-58.2 EndY=-9.8e-15 EndZ=0
    g2: LineSegment StartX=-58.2 StartY=-9.8e-15 StartZ=0 EndX=-53 EndY=-9.8e-15 EndZ=0
    g3: LineSegment StartX=-53 StartY=-9.8e-15 StartZ=0 EndX=-53 EndY=5 EndZ=0
    g4: LineSegment StartX=-67 StartY=5 StartZ=0 EndX=-67 EndY=-9.8e-15 EndZ=0
    g5: LineSegment StartX=-67 StartY=-9.8e-15 StartZ=0 EndX=-61.8 EndY=-9.8e-15 EndZ=0
    g6: LineSegment StartX=-61.8 StartY=-9.8e-15 StartZ=0 EndX=-61.8 EndY=5 EndZ=0
    g7: LineSegment StartX=-61.8 StartY=5 StartZ=0 EndX=-67 EndY=5 EndZ=0
  constraints (24):
    c: Coincident(g0,g1)
    c: Coincident(g1,g2)
    c: Coincident(g2,g3)
    c: Coincident(g3,g0)
    c: Horizontal(g0)
    c: Horizontal(g2)
    c: Vertical(g1)
    c: Vertical(g3)
    c: PointOnObject(g1,g-4)
    c: PointOnObject(g-3,g0)
    c: DistanceX(g0,g-3) = 3
    c: DistanceX(g-3,g0) = 2.2
    c: Coincident(g4,g5)
    c: Coincident(g5,g6)
    c: Coincident(g6,g7)
    c: Coincident(g7,g4)
    c: Vertical(g4)
    c: Vertical(g6)
    c: Horizontal(g5)
    c: Horizontal(g7)
    c: PointOnObject(g5,g-4)
    c: PointOnObject(g-3,g7)
    c: DistanceX(g-3,g6) = 3
    c: DistanceX(g4,g-3) = 2.2
FEATURE [PartDesign::Pad] Pad697
  BaseFeature = -> Chamfer053
  Direction = (0,-1,2e-16)
  Length = 2
  Length2 = 10
  Profile = -> Sketch1070
  ReferenceAxis = -> Sketch1070 [N_Axis]
  Refine = true
  Reversed = true
  Suppressed = false
  Type = 0
FEATURE [Sketcher::SketchObject] Sketch1071
  ArcFitTolerance = 1e-06
  AttachmentSupport = -> [Pad697]
  ExternalGeometry = -> [Pad697]
  FullyConstrained = true
  MakeInternals = false
  MapMode = 5
  Placement = pos=(0,0,5) rot=(0,0,1;0rad)
  sketch-geometry (4):
    g0: LineSegment StartX=-61 StartY=-37 StartZ=0 EndX=-61 EndY=-51 EndZ=0
    g1: LineSegment StartX=-61 StartY=-51 StartZ=0 EndX=-59 EndY=-51 EndZ=0
    g2: LineSegment StartX=-59 StartY=-51 StartZ=0 EndX=-59 EndY=-37 EndZ=0
    g3: LineSegment StartX=-59 StartY=-37 StartZ=0 EndX=-61 EndY=-37 EndZ=0
  constraints (13):
    c: Coincident(g0,g1)
    c: Coincident(g1,g2)
    c: Coincident(g2,g3)
    c: Coincident(g3,g0)
    c: Vertical(g0)
    c: Vertical(g2)
    c: Horizontal(g1)
    c: Horizontal(g3)
    c: DistanceX(g3,g3) = 2
    c: DistanceX(g-5,g-6) = 14
    c: DistanceY(g0,g0) = 14
    c: DistanceY(g-4,g0) = 7
    c: DistanceX(g0,g-4) = 1
FEATURE [PartDesign::Pad] Pad698
  BaseFeature = -> Pad697
  Direction = (0,0,1)
  Length = 5
  Length2 = 10
  Profile = -> Sketch1071
  ReferenceAxis = -> Sketch1071 [N_Axis]
  Refine = true
  Reversed = true
  Suppressed = false
  Type = 0
FEATURE [Sketcher::SketchObject] Sketch1072
  ArcFitTolerance = 1e-06
  AttachmentSupport = -> [Pad698]
  ExternalGeometry = -> [Pad698]
  FullyConstrained = true
  MakeInternals = false
  MapMode = 5
  Placement = pos=(-61,0,0) rot=(0.57735,-0.57735,-0.57735;2.0944rad)
  sketch-geometry (6):
    g0: LineSegment StartX=51 StartY=5 StartZ=0 EndX=51 EndY=0 EndZ=0
    g1: LineSegment StartX=37 StartY=5 StartZ=0 EndX=37 EndY=0 EndZ=0
    g2: LineSegment StartX=51 StartY=5 StartZ=0 EndX=50.5 EndY=5 EndZ=0
    g3: LineSegment StartX=50.5 StartY=5 StartZ=0 EndX=51 EndY=0 EndZ=0
    g4: LineSegment StartX=37 StartY=5 StartZ=0 EndX=37.5 EndY=5 EndZ=0
    g5: LineSegment StartX=37 StartY=0 StartZ=0 EndX=37.5 EndY=5 EndZ=0
  constraints (14):
    c: Coincident(g0,g-5)
    c: Coincident(g0,g-6)
    c: Coincident(g1,g-3)
    c: Coincident(g1,g-4)
    c: Coincident(g2,g0)
    c: Horizontal(g2)
    c: Coincident(g3,g2)
    c: Coincident(g3,g0)
    c: DistanceX(g2,g2) = 0.5
    c: Coincident(g4,g1)
    c: Horizontal(g4)
    c: Coincident(g5,g1)
    c: Coincident(g5,g4)
    c: DistanceX(g4,g4) = 0.5
FEATURE [PartDesign::Pocket] Pocket492
  BaseFeature = -> Pad698
  Direction = (1,0,0)
  Length = 5
  Length2 = 5
  Profile = -> Sketch1072
  ReferenceAxis = -> Sketch1072 [N_Axis]
  Refine = true
  Suppressed = false
  Type = 1
FEATURE [Sketcher::SketchObject] Sketch1073
  ArcFitTolerance = 1e-06
  AttachmentSupport = -> [Pocket492]
  ExternalGeometry = -> [Pocket492]
  FullyConstrained = true
  MakeInternals = false
  MapMode = 5
  Placement = pos=(0,-45,0) rot=(1,0,0;1.5708rad)
  sketch-geometry (6):
    g0: LineSegment StartX=-67 StartY=0 StartZ=0 EndX=-66.5 EndY=5 EndZ=0
    g1: LineSegment StartX=-66.5 StartY=5 StartZ=0 EndX=-67 EndY=5 EndZ=0
    g2: LineSegment StartX=-67 StartY=5 StartZ=0 EndX=-67 EndY=0 EndZ=0
    g3: LineSegment StartX=-53 StartY=0 StartZ=0 EndX=-53.5 EndY=5 EndZ=0
    g4: LineSegment StartX=-53.5 StartY=5 StartZ=0 EndX=-53 EndY=5 EndZ=0
    g5: LineSegment StartX=-53 StartY=5 StartZ=0 EndX=-53 EndY=0 EndZ=0
  constraints (14):
    c: Coincident(g0,g-4)
    c: PointOnObject(g0,g-3)
    c: Coincident(g1,g0)
    c: Coincident(g1,g-4)
    c: Coincident(g2,g1)
    c: Coincident(g2,g0)
    c: Coincident(g3,g-6)
    c: PointOnObject(g3,g-5)
    c: Coincident(g4,g3)
    c: Coincident(g4,g-6)
    c: Coincident(g5,g4)
    c: Coincident(g5,g3)
    c: DistanceX(g1,g1) = 0.5
    c: DistanceX(g4,g4) = 0.5
FEATURE [PartDesign::Pocket] Pocket493
  BaseFeature = -> Pocket492
  Direction = (0,1,-2e-16)
  Length = 5
  Length2 = 5
  Profile = -> Sketch1073
  ReferenceAxis = -> Sketch1073 [N_Axis]
  Refine = true
  Suppressed = false
  Type = 1
FEATURE [Sketcher::SketchObject] Sketch1074
  ArcFitTolerance = 1e-06
  AttachmentSupport = -> [Pocket493]
  ExternalGeometry = -> [Pocket493]
  FullyConstrained = true
  MakeInternals = false
  MapMode = 5
  Placement = pos=(0,0,5) rot=(0,0,1;0rad)
  sketch-geometry (1):
    g0: Circle CenterX=-60 CenterY=-44 CenterZ=0 NormalX=0 NormalY=0 NormalZ=1 AngleXU=0 Radius=2.5
  constraints (2):
    c: Coincident(g0,g-4)
    c: Equal(g0,g-4)
FEATURE [PartDesign::Pad] Pad699
  BaseFeature = -> Pocket493
  Direction = (0,0,1)
  Length = 1
  Length2 = 10
  Profile = -> Sketch1074
  ReferenceAxis = -> Sketch1074 [N_Axis]
  Refine = true
  Suppressed = false
  Type = 0
FEATURE [Sketcher::SketchObject] Sketch1075
  ArcFitTolerance = 1e-06
  AttachmentSupport = -> [Pad699]
  ExternalGeometry = -> [Pad699]
  FullyConstrained = true
  MakeInternals = false
  MapMode = 5
  Placement = pos=(0,0,6) rot=(0,0,1;0rad)
  sketch-geometry (1):
    g0: Circle CenterX=-60 CenterY=-44 CenterZ=0 NormalX=0 NormalY=0 NormalZ=1 AngleXU=0 Radius=4.05
  constraints (2):
    c: Coincident(g0,g-3)
    c: Diameter(g0) = 8.1
FEATURE [PartDesign::Pad] Pad700
  BaseFeature = -> Pad699
  Direction = (0,0,1)
  Length = 3
  Length2 = 10
  Profile = -> Sketch1075
  ReferenceAxis = -> Sketch1075 [N_Axis]
  Refine = true
  Suppressed = false
  Type = 0
FEATURE [Sketcher::SketchObject] Sketch1076
  ArcFitTolerance = 1e-06
  AttachmentSupport = -> [Pad700]
  ExternalGeometry = -> [Pad700]
  FullyConstrained = true
  MakeInternals = false
  MapMode = 5
  Placement = pos=(-59,0,0) rot=(0.57735,0.57735,0.57735;2.0944rad)
  sketch-geometry (9):
    g0: LineSegment StartX=-48.55 StartY=8.33333 StartZ=0 EndX=-48.55 EndY=7.83333 EndZ=0
    g1: LineSegment StartX=-48.55 StartY=7.83333 StartZ=0 EndX=-47.55 EndY=7.83333 EndZ=0
    g2: LineSegment StartX=-47.55 StartY=7.83333 StartZ=0 EndX=-47.55 EndY=8.33333 EndZ=0
    g3: LineSegment StartX=-47.55 StartY=8.33333 StartZ=0 EndX=-48.55 EndY=8.33333 EndZ=0
    g4: LineSegment StartX=-48.55 StartY=7.16667 StartZ=0 EndX=-48.55 EndY=6.66667 EndZ=0
    g5: LineSegment StartX=-48.55 StartY=6.66667 StartZ=0 EndX=-47.55 EndY=6.66667 EndZ=0
    g6: LineSegment StartX=-47.55 StartY=6.66667 StartZ=0 EndX=-47.55 EndY=7.16667 EndZ=0
    g7: LineSegment StartX=-47.55 StartY=7.16667 StartZ=0 EndX=-48.55 EndY=7.16667 EndZ=0
    g8: LineSegment [constr] StartX=-48.55 StartY=7.83333 StartZ=0 EndX=-48.55 EndY=7.16667 EndZ=0
  constraints (28):
    c: Coincident(g0,g1)
    c: Coincident(g1,g2)
    c: Coincident(g2,g3)
    c: Coincident(g3,g0)
    c: Vertical(g0)
    c: Vertical(g2)
    c: Horizontal(g1)
    c: Horizontal(g3)
    c: Coincident(g4,g5)
    c: Coincident(g5,g6)
    c: Coincident(g6,g7)
    c: Coincident(g7,g4)
    c: Vertical(g4)
    c: Vertical(g6)
    c: Horizontal(g5)
    c: Horizontal(g7)
    c: DistanceY(g-3,g-3) = 3
    c: DistanceY(g0,g0) = 0.5
    c: DistanceY(g4,g4) = 0.5
    c: DistanceX(g0,g-4) = 0.5
    c: Coincident(g8,g0)
    c: Coincident(g8,g4)
    c: Vertical(g8)
    c: DistanceX(g1,g1) = 1
    c: DistanceX(g5,g5) = 1
    c: DistanceY(g4,g0) = 0.666667
    c: DistanceY(g0,g-4) = 0.666667
    c: DistanceY(g-5,g4) = 0.666666
FEATURE [PartDesign::Groove] Groove002
  Angle = 360
  Angle2 = 60
  Axis = (0,0,1)
  Base = (-60,-44,9)
  BaseFeature = -> Pad700
  Profile = -> Sketch1076
  ReferenceAxis = -> Pad700 [Edge115]
  Refine = true
  Reversed = true
  Suppressed = false
  Type = 0
FEATURE [Sketcher::SketchObject] Sketch1077
  ArcFitTolerance = 1e-06
  AttachmentSupport = -> [Groove002]
  ExternalGeometry = -> [Groove002]
  FullyConstrained = true
  MakeInternals = false
  MapMode = 5
  Placement = pos=(-59,0,0) rot=(0.57735,0.57735,0.57735;2.0944rad)
  sketch-geometry (7):
    g0: LineSegment StartX=-48.05 StartY=9 StartZ=0 EndX=-45.125 EndY=22.4 EndZ=0
    g1: LineSegment StartX=-39.95 StartY=9 StartZ=0 EndX=-42.875 EndY=22.4 EndZ=0
    g2: LineSegment StartX=-42.875 StartY=22.4 StartZ=0 EndX=-45.125 EndY=22.4 EndZ=0
    g3: LineSegment StartX=-44 StartY=9 StartZ=0 EndX=-44 EndY=22.4 EndZ=0
    g4: LineSegment StartX=-45.5179 StartY=20.6 StartZ=0 EndX=-42.4821 EndY=20.6 EndZ=0
    g5: LineSegment StartX=-47.55 StartY=9 StartZ=0 EndX=-45.0179 EndY=20.6 EndZ=0
    g6: LineSegment StartX=-42.9821 StartY=20.6 StartZ=0 EndX=-40.45 EndY=9 EndZ=0
  constraints (23):
    c: Coincident(g0,g-3)
    c: Coincident(g1,g-3)
    c: Coincident(g2,g1)
    c: Coincident(g2,g0)
    c: Horizontal(g2)
    c: DistanceY(g0,g0) = 13.4
    c: DistanceX(g2,g2) = 2.25
    c: Symmetric(g-3,g-3,g3)
    c: Symmetric(g2,g2,g3)
    c: Vertical(g3)
    c: PointOnObject(g4,g0)
    c: PointOnObject(g4,g1)
    c: Horizontal(g4)
    c: DistanceY(g0,g4) = 11.6
    c: DistanceY(g4,g1) = 1.8
    c: PointOnObject(g5,g-3)
    c: PointOnObject(g5,g4)
    c: PointOnObject(g6,g4)
    c: PointOnObject(g6,g-3)
    c: Parallel(g6,g1)
    c: Parallel(g5,g0)
    c: DistanceX(g6,g1) = 0.5
    c: DistanceX(g0,g5) = 0.5
FEATURE [Sketcher::SketchObject] Sketch1078
  ArcFitTolerance = 1e-06
  AttachmentSupport = -> [Groove002]
  ExternalGeometry = -> [Groove002,Sketch1077]
  FullyConstrained = true
  MakeInternals = false
  MapMode = 5
  Placement = pos=(0,0,9) rot=(0,0,1;0rad)
  sketch-geometry (1):
    g0: Circle CenterX=-60 CenterY=-44 CenterZ=0 NormalX=0 NormalY=0 NormalZ=1 AngleXU=0 Radius=3.68816
  constraints (2):
    c: Coincident(g0,g-3)
    c: PointOnObject(g-4,g0)
FEATURE [PartDesign::Pad] Pad701
  BaseFeature = -> Groove002
  Direction = (0,0,1)
  Length = 1
  Length2 = 10
  Profile = -> Sketch1078
  ReferenceAxis = -> Sketch1078 [N_Axis]
  Refine = true
  Suppressed = false
  Type = 0
FEATURE [Sketcher::SketchObject] Sketch1079
  ArcFitTolerance = 1e-06
  AttachmentSupport = -> [Pad701]
  ExternalGeometry = -> [Pad701,Sketch1077]
  FullyConstrained = false
  MakeInternals = false
  MapMode = 5
  Placement = pos=(0,0,10) rot=(0,0,1;0rad)
  sketch-geometry (1):
    g0: Circle CenterX=-60 CenterY=-44 CenterZ=0 NormalX=0 NormalY=0 NormalZ=1 AngleXU=0 Radius=3.95
  constraints (1):
    c: Radius(g0) = 3.95
FEATURE [PartDesign::Pad] Pad702
  BaseFeature = -> Pad701
  Direction = (0,0,1)
  Length = 1.5
  Length2 = 10
  Profile = -> Sketch1079
  ReferenceAxis = -> Sketch1079 [N_Axis]
  Refine = true
  Suppressed = false
  Type = 0
FEATURE [Sketcher::SketchObject] Sketch1080
  ArcFitTolerance = 1e-06
  AttachmentSupport = -> [Pad702]
  ExternalGeometry = -> [Pad702,Sketch1077]
  FullyConstrained = true
  MakeInternals = false
  MapMode = 5
  Placement = pos=(0,0,11.5) rot=(0,0,1;0rad)
  sketch-geometry (1):
    g0: Circle CenterX=-60 CenterY=-44 CenterZ=0 NormalX=0 NormalY=0 NormalZ=1 AngleXU=0 Radius=3.17
  constraints (2):
    c: Coincident(g0,g-3)
    c: Radius(g0) = 3.17
FEATURE [PartDesign::Pad] Pad703
  BaseFeature = -> Pad702
  Direction = (0,0,1)
  Length = 1
  Length2 = 10
  Profile = -> Sketch1080
  ReferenceAxis = -> Sketch1080 [N_Axis]
  Refine = true
  Suppressed = false
  Type = 0
FEATURE [Sketcher::SketchObject] Sketch1081
  ArcFitTolerance = 1e-06
  AttachmentSupport = -> [Pad703]
  ExternalGeometry = -> [Pad703]
  FullyConstrained = true
  MakeInternals = false
  MapMode = 5
  Placement = pos=(0,0,12.5) rot=(0,0,1;0rad)
  sketch-geometry (1):
    g0: Circle CenterX=-60 CenterY=-44 CenterZ=0 NormalX=0 NormalY=0 NormalZ=1 AngleXU=0 Radius=3.4
  constraints (2):
    c: Coincident(g0,g-3)
    c: Radius(g0) = 3.4
FEATURE [PartDesign::Pad] Pad704
  BaseFeature = -> Pad703
  Direction = (0,0,1)
  Length = 1.5
  Length2 = 10
  Profile = -> Sketch1081
  ReferenceAxis = -> Sketch1081 [N_Axis]
  Refine = true
  Suppressed = false
  Type = 0
FEATURE [Sketcher::SketchObject] Sketch1082
  ArcFitTolerance = 1e-06
  AttachmentSupport = -> [Pad704]
  ExternalGeometry = -> [Pad704]
  FullyConstrained = true
  MakeInternals = false
  MapMode = 5
  Placement = pos=(0,0,14) rot=(0,0,1;0rad)
  sketch-geometry (1):
    g0: Circle CenterX=-60 CenterY=-44 CenterZ=0 NormalX=0 NormalY=0 NormalZ=1 AngleXU=0 Radius=2.65
  constraints (2):
    c: Coincident(g0,g-3)
    c: Radius(g0) = 2.65
FEATURE [PartDesign::Pad] Pad705
  BaseFeature = -> Pad704
  Direction = (0,0,1)
  Length = 1
  Length2 = 10
  Profile = -> Sketch1082
  ReferenceAxis = -> Sketch1082 [N_Axis]
  Refine = true
  Suppressed = false
  Type = 0
FEATURE [Sketcher::SketchObject] Sketch1083
  ArcFitTolerance = 1e-06
  AttachmentSupport = -> [Pad705]
  ExternalGeometry = -> [Pad705]
  FullyConstrained = true
  MakeInternals = false
  MapMode = 5
  Placement = pos=(0,0,15) rot=(0,0,1;0rad)
  sketch-geometry (1):
    g0: Circle CenterX=-60 CenterY=-44 CenterZ=0 NormalX=0 NormalY=0 NormalZ=1 AngleXU=0 Radius=2.93
  constraints (2):
    c: Coincident(g0,g-3)
    c: Radius(g0) = 2.93
FEATURE [PartDesign::Pad] Pad706
  BaseFeature = -> Pad705
  Direction = (0,0,1)
  Length = 1.5
  Length2 = 10
  Profile = -> Sketch1083
  ReferenceAxis = -> Sketch1083 [N_Axis]
  Refine = true
  Suppressed = false
  Type = 0
FEATURE [Sketcher::SketchObject] Sketch1084
  ArcFitTolerance = 1e-06
  AttachmentSupport = -> [Pad706]
  ExternalGeometry = -> [Pad706]
  FullyConstrained = true
  MakeInternals = false
  MapMode = 5
  Placement = pos=(0,0,16.5) rot=(0,0,1;0rad)
  sketch-geometry (1):
    g0: Circle CenterX=-60 CenterY=-44 CenterZ=0 NormalX=0 NormalY=0 NormalZ=1 AngleXU=0 Radius=2.15
  constraints (2):
    c: Coincident(g0,g-3)
    c: Radius(g0) = 2.15
FEATURE [PartDesign::Body] Body053  label="Drill_Fist1"
  AllowCompound = false
  Group = -> [Sketch1064,Pad691,Sketch1065,Pad692,Sketch1066,Pad693,Sketch1067,Pad694,Sketch1068,Pad695,Sketch1069,Pad696,Chamfer052,Chamfer053,Sketch1070,Pad697,Sketch1071,Pad698,Sketch1072,Pocket492,Sketch1073,Pocket493,Sketch1074,Pad699,Sketch1075,Pad700,Sketch1076,Groove002,Sketch1077,Sketch1078,Pad701,Sketch1079,Pad702,Sketch1080,Pad703,Sketch1081,Pad704,Sketch1082,Pad705,Sketch1083,Pad706,Sketch1084,+10 more]
  Origin = -> Origin058
  Placement = pos=(-57,2,-66) rot=(0,1,0;1.5708rad)
  Tip = -> Fillet025
COMPONENT P3 — geometry summary ("Leg_Connector"; its construction recipe is too large to include in this document):
  bounding box: 73.8 x 54.0 x 24.3 mm
  tessellated surface: 21,372 triangles
  volume: 9004 mm^3 (9% of its bounding box)
COMPONENT P4 — geometry summary ("Head"; its construction recipe is too large to include in this document):
  bounding box: 50.2 x 45.1 x 39.2 mm
  tessellated surface: 20,145 triangles
  volume: 10286 mm^3 (12% of its bounding box)
COMPONENT P5 — geometry summary ("Left_Arm"; its construction recipe is too large to include in this document):
  bounding box: 65.0 x 23.7 x 21.0 mm
  tessellated surface: 21,550 triangles
  volume: 7838 mm^3 (24% of its bounding box)
COMPONENT P6 — geometry summary ("Right_Arm"; its construction recipe is too large to include in this document):
  bounding box: 65.0 x 23.7 x 20.8 mm
  tessellated surface: 20,752 triangles
  volume: 7798 mm^3 (24% of its bounding box)
PROVENANCE & LICENSES
A FreeCAD (.FCStd) document from a public repository crawl; recipes are the document's own serialized feature recipes (and, for linked parts, companion documents' recipes).
License: as declared in the source repository (recorded in the dataset sidecar).
